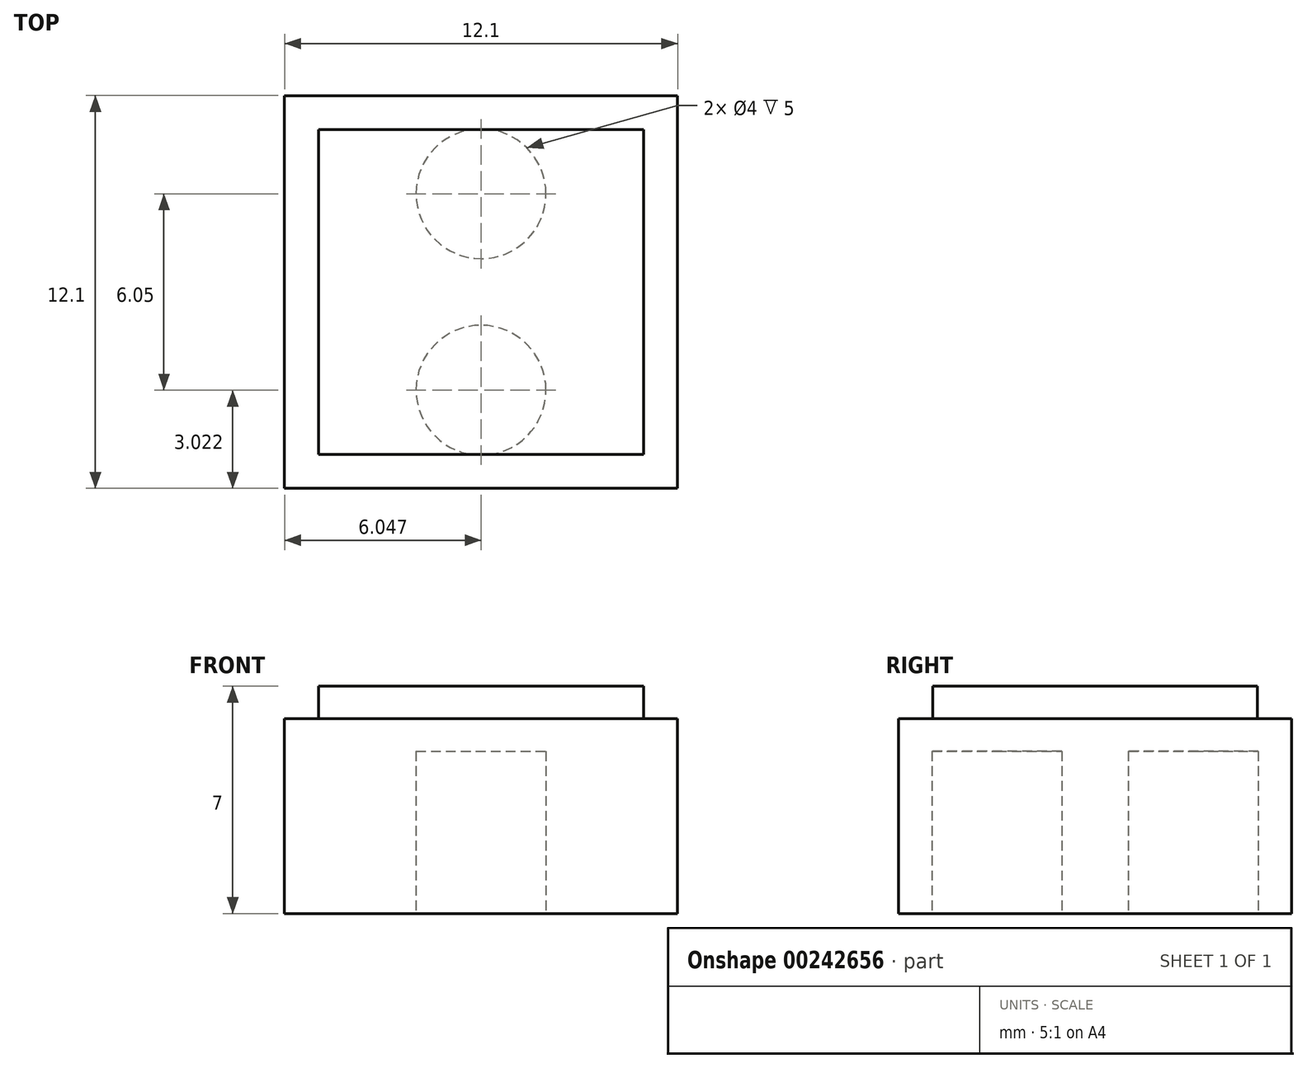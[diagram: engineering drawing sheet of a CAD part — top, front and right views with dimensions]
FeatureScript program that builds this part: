
annotation { "Feature Type Name" : "Feature", "Feature Type Description" : "" }
export const myFeature = defineFeature(function(context is Context, id is Id, definition is map)
    precondition{}
    {
        {
            var Q0;
            Q0=qCreatedBy(makeId("Top.planeOp"),FACE);
            var sketch = newSketch(context, id + "F0", { "sketchPlane" : qUnion([Q0])});
            skLineSegment(sketch, "E0.bottom", {"start": v(-45.84, 12.33) * mm, "end": v(-33.74, 12.33) * mm});
            skLineSegment(sketch, "E0.top", {"start": v(-45.84, 0.23) * mm, "end": v(-33.74, 0.23) * mm});
            skLineSegment(sketch, "E0.left", {"start": v(-45.84, 12.33) * mm, "end": v(-45.84, 0.23) * mm});
            skLineSegment(sketch, "E0.right", {"start": v(-33.74, 12.33) * mm, "end": v(-33.74, 0.23) * mm});
            skPoint(sketch, "E0.middle", {"position": v(-39.8, 6.28) * mm});
            skSolve(sketch);
        }
        {
            var Q0;
            Q0 = qSketchRegion(id + "F0", true);
            extrude(context, id + "F1", {"entities" : qUnion([Q0]), "depth" : 6 * mm});
        }
        {
            var Q0;
            Q0=makeQuery(id+"F1.opExtrude","CAP_FACE",FACE,{"disambiguationData":[OSD([sQuery(id+"F0.wireOp",EDGE,"E0.bottom"),sQuery(id+"F0.wireOp",EDGE,"E0.top"),sQuery(id+"F0.wireOp",EDGE,"E0.left"),sQuery(id+"F0.wireOp",EDGE,"E0.right")])],"isStart":true});
            var sketch = newSketch(context, id + "F2", { "sketchPlane" : qUnion([Q0])});
            skCircle(sketch, "E1", {"center": v(-39.8, -3.25) * mm, "radius": 2 * mm});
            skCircle(sketch, "E2", {"center": v(-39.8, -9.3) * mm, "radius": 2 * mm});
            skSolve(sketch);
        }
        {
            var Q0;
            Q0=makeQuery(id+"F2.imprint","IMPRINT",FACE,{"disambiguationData":[TD([[makeQuery(id+"F2.imprint","IMPRINT",EDGE,{"derivedFrom":sQuery(id+"F2.wireOp",EDGE,"E1")}),1.0]])]});
            var Q1;
            Q1=makeQuery(id+"F2.imprint","IMPRINT",FACE,{"disambiguationData":[TD([[makeQuery(id+"F2.imprint","IMPRINT",EDGE,{"derivedFrom":sQuery(id+"F2.wireOp",EDGE,"E2")}),1.0]])]});
            extrude(context, id + "F3", {"entities" : qUnion([Q0, Q1]), "operationType" : NewBodyOperationType.REMOVE, "oppositeDirection" : true, "depth" : 5 * mm});
        }
        {
            var Q0;
            Q0=makeQuery(id+"F1.opExtrude","CAP_FACE",FACE,{"disambiguationData":[OSD([sQuery(id+"F0.wireOp",EDGE,"E0.bottom"),sQuery(id+"F0.wireOp",EDGE,"E0.top"),sQuery(id+"F0.wireOp",EDGE,"E0.left"),sQuery(id+"F0.wireOp",EDGE,"E0.right")])],"isStart":false});
            var sketch = newSketch(context, id + "F4", { "sketchPlane" : qUnion([Q0])});
            skLineSegment(sketch, "E3.bottom", {"start": v(-44.8, 11.28) * mm, "end": v(-34.8, 11.28) * mm});
            skLineSegment(sketch, "E3.top", {"start": v(-44.8, 1.28) * mm, "end": v(-34.8, 1.28) * mm});
            skLineSegment(sketch, "E3.left", {"start": v(-44.8, 11.28) * mm, "end": v(-44.8, 1.28) * mm});
            skLineSegment(sketch, "E3.right", {"start": v(-34.8, 11.28) * mm, "end": v(-34.8, 1.28) * mm});
            skPoint(sketch, "E3.middle", {"position": v(-39.8, 6.28) * mm});
            skPoint(sketch, "E3.middle.positionSnap0", {"position": v(-39.8, 12.33) * mm});
            skPoint(sketch, "E3.middle.positionSnap1", {"position": v(-45.84, 6.28) * mm});
            skPoint(sketch, "E3.centerSnap0", {"position": v(-39.8, 12.33) * mm});
            skPoint(sketch, "E3.centerSnap1", {"position": v(-45.84, 6.28) * mm});
            skSolve(sketch);
        }
        {
            var Q0;
            Q0 = qSketchRegion(id + "F4", true);
            extrude(context, id + "F5", {"entities" : qUnion([Q0]), "operationType" : NewBodyOperationType.ADD, "depth" : 1 * mm});
        }
    });
